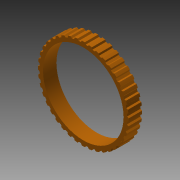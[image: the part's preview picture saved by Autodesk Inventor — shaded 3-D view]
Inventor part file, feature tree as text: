
AUTODESK INVENTOR PART (.ipt)
format: ipt  version: 2013 (Build 170138000, 138)  size: 271,360 bytes
history: native  units: in
note: dims shown in document units (in); Inventor stores cm internally (conversion verified against a paired STEP export)
features: extrude x1, sketch x1
ambient origin geometry x8: Origin, YZ Plane, XZ Plane, XY Plane, X Axis, Y Axis, Z Axis, Center Point
bodies: Solid1 (feature_tree)
feature tree (2):
  extrude  "Extrusion1"  [1 undecoded]
  sketch  "Sketch1"  dims[d0=0.9in d1=0.0in]
note: 1 required parameter value undecoded (feature->parameter linkage not recoverable at this tier; creation-order binding heuristic only, values carry confidence <= 0.55)
